# Revit family: T3
name_source: partatom
category: Lighting Fixtures
units: mm (PartAtom-declared; Revit-internal decimal feet)

## family parameters
Cut with Voids When Loaded = No
Host = Face
Light Source = Yes
OmniClass Number = 23.80.70.14.21
OmniClass Title = Street and Roadway Lighting
Part Type = Normal
Room Calculation Point = No
Round Connector Dimension = Use Diameter
Shared = No

## types (1)
- T3
    Apparent Load = 55 VA
    Assembly Code = D5020280
    CRI = 70
    Certification = Listed to UL8750 , UL1598 and CSA22.2#250.13-14 for wet locations
    Color Filter = 16777215
    Controls = occupancy sensors, external dimmers, etc
    Default Elevation = 48 "
    Description = The stacked top of the Monaco T3 pays reference to historic gas lantern themes with the modularity of the Village Collection Series of decorative post tops. The Village Collection Series has over 80 different configurable combinations available for lighting designers and architects to create the perfect post top for their environment
    Dimming Lamp Color Temperature Shift = <None>
    Emit Shape Visible in Rendering = No
    Emit from Circle Diameter = 10 "
    Finish = Metal-Galvanized_Steel
    Glass = Glass
    IP Rating = IP55
    Lamp = LED
    Light Distribution = IES Type II,III,IV
    Lighting Connector Description = Lighting Connector
    Load Classification = Lighting
    Manufacturer = Beacon Products
    Model = Monaco
    Model Type = Single fixture
    Photometric Web File = generic
    Power Factor = 1
    Sensor Type = Occupancy Sensor
    Tilt Angle = 60.00°
    Type Comments = Light Fixture
    URL = https://www.currentlighting.com
    Voltage = 120 V
    Warranty = 5 Year Limited Warranty
    Wattage Comments = 55W
    Watts = 55 W

## geometry (parser evidence)
native form markers: Sweep x7
no freeform markers — native parametric forms only
